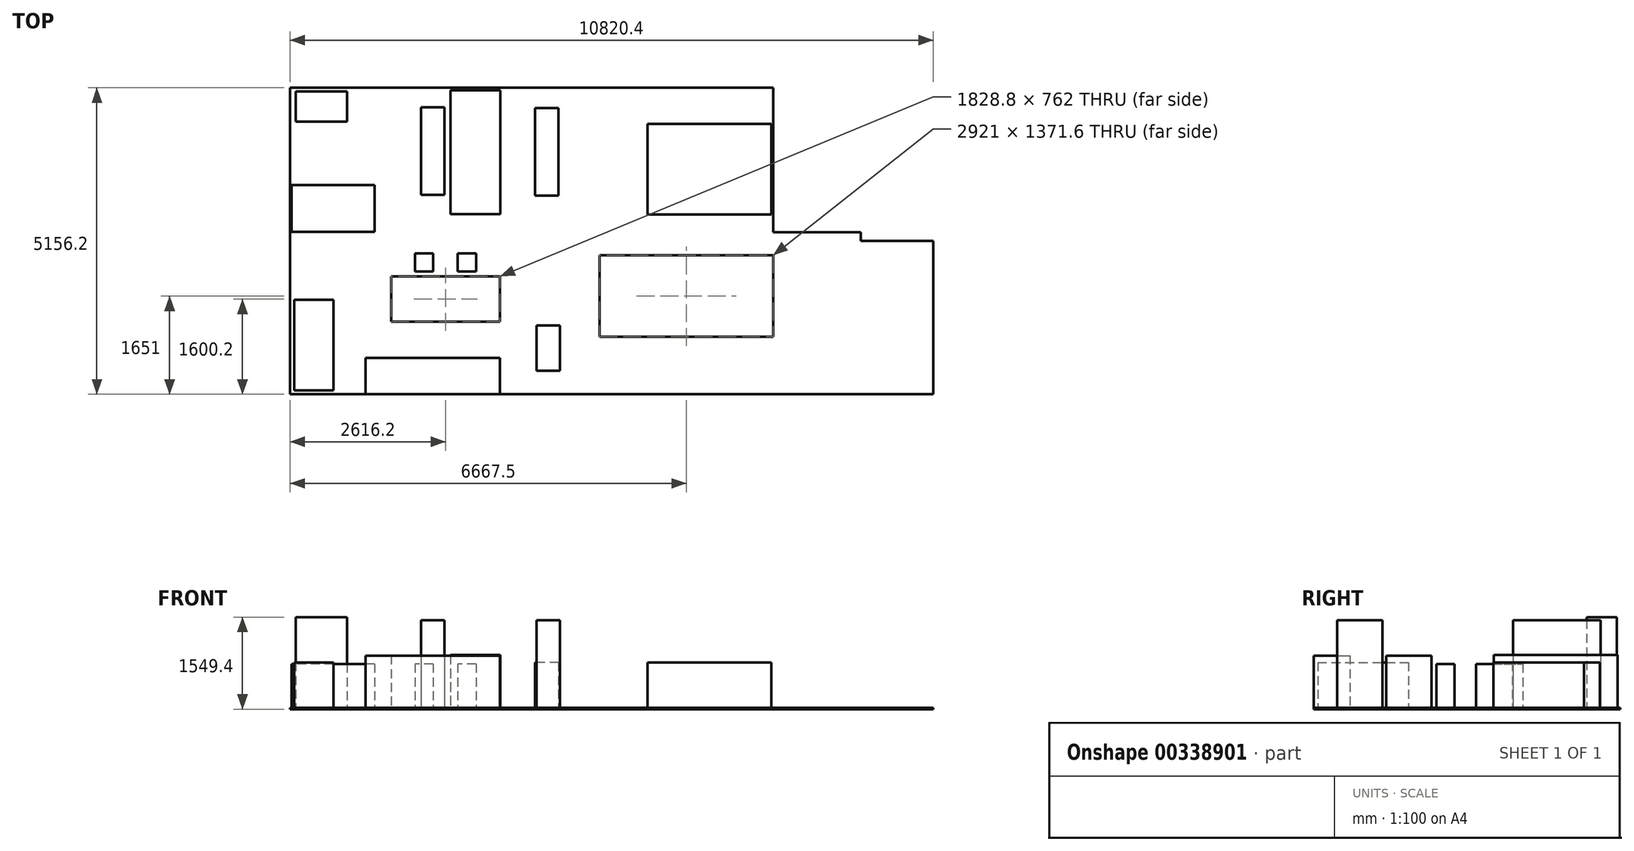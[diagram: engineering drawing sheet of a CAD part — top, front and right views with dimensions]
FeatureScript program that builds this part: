
annotation { "Feature Type Name" : "Feature", "Feature Type Description" : "" }
export const myFeature = defineFeature(function(context is Context, id is Id, definition is map)
    precondition{}
    {
        {
            var Q0;
            Q0=qCreatedBy(makeId("Top.planeOp"),FACE);
            var sketch = newSketch(context, id + "F0", { "sketchPlane" : qUnion([Q0])});
            skLineSegment(sketch, "E0.bottom", {"start": v(4800.6, -2578.1) * mm, "end": v(-812.8, -2578.1) * mm});
            skLineSegment(sketch, "E0.top", {"start": v(3327.4, 2578.1) * mm, "end": v(-4800.6, 2578.1) * mm});
            skLineSegment(sketch, "E0.left", {"start": v(4800.6, -2578.1) * mm, "end": v(4800.6, 0) * mm});
            skLineSegment(sketch, "E0.right", {"start": v(-4800.6, -2578.1) * mm, "end": v(-4800.6, 2578.1) * mm});
            skPoint(sketch, "E0.middle", {"position": v(0, 0) * mm});
            skLineSegment(sketch, "E1", {"start": v(-203.2, 2578.1) * mm, "end": v(-203.2, 139.7) * mm});
            skLineSegment(sketch, "E2", {"start": v(-203.2, 139.7) * mm, "end": v(406.4, 139.7) * mm});
            skLineSegment(sketch, "E3", {"start": v(406.4, 139.7) * mm, "end": v(406.4, 2578.1) * mm});
            skLineSegment(sketch, "E4", {"start": v(-1270, -2578.1) * mm, "end": v(-1270, -952.5) * mm});
            skLineSegment(sketch, "E5", {"start": v(-1270, -952.5) * mm, "end": v(-812.8, -952.5) * mm});
            skLineSegment(sketch, "E6", {"start": v(-812.8, -952.5) * mm, "end": v(-812.8, -2578.1) * mm});
            skLineSegment(sketch, "E7", {"start": v(4800.6, -2578.1) * mm, "end": v(6019.8, -2578.1) * mm});
            skLineSegment(sketch, "E8", {"start": v(6019.8, -2578.1) * mm, "end": v(6019.8, 0) * mm});
            skLineSegment(sketch, "E9", {"start": v(6019.8, 0) * mm, "end": v(4800.6, 0) * mm});
            skLineSegment(sketch, "E10", {"start": v(406.4, 139.7) * mm, "end": v(406.4, -1612.9) * mm});
            skLineSegment(sketch, "E11", {"start": v(406.4, -1612.9) * mm, "end": v(4800.6, -1612.9) * mm});
            skLineSegment(sketch, "E12", {"start": v(-1270, -952.5) * mm, "end": v(-1270, -596.9) * mm});
            skLineSegment(sketch, "E13", {"start": v(-1270, -596.9) * mm, "end": v(-3098.8, -596.9) * mm});
            skLineSegment(sketch, "E14", {"start": v(-3098.8, -596.9) * mm, "end": v(-3098.8, -1358.9) * mm});
            skLineSegment(sketch, "E15", {"start": v(-3098.8, -1358.9) * mm, "end": v(-1270, -1358.9) * mm});
            skLineSegment(sketch, "E16", {"start": v(-3530.6, -2578.1) * mm, "end": v(-3530.6, -1968.5) * mm});
            skLineSegment(sketch, "E17", {"start": v(-3530.6, -1968.5) * mm, "end": v(-1270, -1968.5) * mm});
            skLineSegment(sketch, "E18", {"start": v(3327.4, -1612.9) * mm, "end": v(3327.4, 144.58) * mm});
            skLineSegment(sketch, "E19", {"start": v(3327.4, 144.58) * mm, "end": v(3327.4, 144.58) * mm});
            skPoint(sketch, "E20.orphan", {"position": v(4800.6, 2578.1) * mm});
            skLineSegment(sketch, "E21", {"start": v(3327.4, 144.58) * mm, "end": v(4800.6, 144.58) * mm});
            skLineSegment(sketch, "E22", {"start": v(4800.6, 0) * mm, "end": v(4800.6, 144.58) * mm});
            skLineSegment(sketch, "E23", {"start": v(-812.8, -2578.1) * mm, "end": v(-1270, -2578.1) * mm});
            skLineSegment(sketch, "E24", {"start": v(-1270, -2578.1) * mm, "end": v(-4800.6, -2578.1) * mm});
            skLineSegment(sketch, "E25", {"start": v(3327.4, 144.58) * mm, "end": v(3327.4, 2578.1) * mm});
            skLineSegment(sketch, "E26", {"start": v(406.4, 139.7) * mm, "end": v(406.4, 139.7) * mm});
            skLineSegment(sketch, "E27", {"start": v(406.4, -241.3) * mm, "end": v(3327.4, -241.3) * mm});
            skPoint(sketch, "E27.endSnap0", {"position": v(3327.4, -734.16) * mm});
            skSolve(sketch);
        }
        {
            var Q0;
            Q0=sQuery(id+"F0.wireOp",EDGE,"E0.top");
            var Q1;
            Q1=sQuery(id+"F0.wireOp",EDGE,"E0.right");
            var Q2;
            Q2=sQuery(id+"F0.wireOp",EDGE,"E24");
            var Q3;
            Q3=sQuery(id+"F0.wireOp",EDGE,"E4");
            var Q4;
            Q4=sQuery(id+"F0.wireOp",EDGE,"E5");
            var Q5;
            Q5=sQuery(id+"F0.wireOp",EDGE,"E6");
            var Q6;
            Q6=sQuery(id+"F0.wireOp",EDGE,"E0.bottom");
            var Q7;
            Q7=sQuery(id+"F0.wireOp",EDGE,"E7");
            var Q8;
            Q8=sQuery(id+"F0.wireOp",EDGE,"E8");
            var Q9;
            Q9=sQuery(id+"F0.wireOp",EDGE,"E9");
            var Q10;
            Q10=sQuery(id+"F0.wireOp",EDGE,"E22");
            var Q11;
            Q11=sQuery(id+"F0.wireOp",EDGE,"E21");
            var Q12;
            Q12=sQuery(id+"F0.wireOp",EDGE,"E25");
            extrude(context, id + "F1", {"bodyType" : ToolBodyType.SURFACE, "surfaceEntities" : qUnion([Q0, Q1, Q2, Q3, Q4, Q5, Q6, Q7, Q8, Q9, Q10, Q11, Q12]), "depth" : 2133.6 * mm});
        }
        {
            var Q0;
            {var subQ0=sQuery(id+"F0.wireOp",EDGE,"E12");Q0=makeQuery(id+"F0.imprint","IMPRINT",FACE,{"disambiguationData":[TD([[makeQuery(id+"F0.imprint","IMPRINT",EDGE,{"derivedFrom":subQ0}),1.0]])]});}
            var Q1;
            {var subQ4=sQuery(id+"F0.wireOp",EDGE,"E16");Q1=makeQuery(id+"F0.imprint","IMPRINT",FACE,{"disambiguationData":[TD([[makeQuery(id+"F0.imprint","IMPRINT",EDGE,{"derivedFrom":subQ4}),-1.0]])]});}
            extrude(context, id + "F2", {"entities" : qUnion([Q0, Q1]), "depth" : 901.7 * mm});
        }
        {
            var Q0;
            Q0=sQuery(id+"F0.wireOp",EDGE,"E1");
            var Q1;
            Q1=sQuery(id+"F0.wireOp",EDGE,"E2");
            var Q2;
            Q2=sQuery(id+"F0.wireOp",EDGE,"E3");
            extrude(context, id + "F3", {"bodyType" : ToolBodyType.SURFACE, "surfaceEntities" : qUnion([Q0, Q1, Q2]), "depth" : 2133.6 * mm});
        }
        {
            var Q0;
            Q0 = qSketchRegion(id + "F0", true);
            extrude(context, id + "F4", {"entities" : qUnion([Q0]), "depth" : 25.4 * mm});
        }
        {
            var Q0;
            Q0=sQuery(id+"F0.wireOp",EDGE,"E10");
            var Q1;
            Q1=sQuery(id+"F0.wireOp",EDGE,"E11");
            extrude(context, id + "F5", {"bodyType" : ToolBodyType.SURFACE, "surfaceEntities" : qUnion([Q0, Q1]), "depth" : 2133.6 * mm});
        }
        {
            var Q0;
            Q0=sQuery(id+"F0.wireOp",EDGE,"E18");
            extrude(context, id + "F6", {"bodyType" : ToolBodyType.SURFACE, "surfaceEntities" : qUnion([Q0]), "depth" : 2133.6 * mm});
        }
        {
            var Q0;
            Q0=makeQuery(id+"F4.opExtrude","CAP_FACE",FACE,{"disambiguationData":[OSD([sQuery(id+"F0.wireOp",EDGE,"E0.bottom"),sQuery(id+"F0.wireOp",EDGE,"E0.top"),sQuery(id+"F0.wireOp",EDGE,"E0.right"),sQuery(id+"F0.wireOp",EDGE,"E4"),sQuery(id+"F0.wireOp",EDGE,"E7"),sQuery(id+"F0.wireOp",EDGE,"E8"),sQuery(id+"F0.wireOp",EDGE,"E9"),sQuery(id+"F0.wireOp",EDGE,"E12"),sQuery(id+"F0.wireOp",EDGE,"E13"),sQuery(id+"F0.wireOp",EDGE,"E14"),sQuery(id+"F0.wireOp",EDGE,"E15"),sQuery(id+"F0.wireOp",EDGE,"E21"),sQuery(id+"F0.wireOp",EDGE,"E22"),sQuery(id+"F0.wireOp",EDGE,"E23"),sQuery(id+"F0.wireOp",EDGE,"E24"),sQuery(id+"F0.wireOp",EDGE,"E25")])],"isStart":false});
            var sketch = newSketch(context, id + "F7", { "sketchPlane" : qUnion([Q0])});
            skLineSegment(sketch, "E28.bottom", {"start": v(-1265.13, 450.06) * mm, "end": v(-2103.33, 450.06) * mm});
            skLineSegment(sketch, "E28.top", {"start": v(-1265.13, 2532.86) * mm, "end": v(-2103.33, 2532.86) * mm});
            skLineSegment(sketch, "E28.left", {"start": v(-1265.13, 450.06) * mm, "end": v(-1265.13, 2532.86) * mm});
            skLineSegment(sketch, "E28.right", {"start": v(-2103.33, 450.06) * mm, "end": v(-2103.33, 2532.86) * mm});
            skPoint(sketch, "E28.middle", {"position": v(-1684.23, 1491.46) * mm});
            skSolve(sketch);
        }
        {
            var Q0;
            Q0=makeQuery(id+"F7.imprint","IMPRINT",FACE,{"disambiguationData":[TD([[makeQuery(id+"F7.imprint","IMPRINT",EDGE,{"derivedFrom":sQuery(id+"F7.wireOp",EDGE,"E28.bottom")}),-1.0]])]});
            extrude(context, id + "F8", {"entities" : qUnion([Q0]), "depth" : 889 * mm});
        }
        {
            var Q0;
            Q0=makeQuery(id+"F4.opExtrude","CAP_FACE",FACE,{"disambiguationData":[OSD([sQuery(id+"F0.wireOp",EDGE,"E0.bottom"),sQuery(id+"F0.wireOp",EDGE,"E0.top"),sQuery(id+"F0.wireOp",EDGE,"E0.right"),sQuery(id+"F0.wireOp",EDGE,"E4"),sQuery(id+"F0.wireOp",EDGE,"E7"),sQuery(id+"F0.wireOp",EDGE,"E8"),sQuery(id+"F0.wireOp",EDGE,"E9"),sQuery(id+"F0.wireOp",EDGE,"E12"),sQuery(id+"F0.wireOp",EDGE,"E13"),sQuery(id+"F0.wireOp",EDGE,"E14"),sQuery(id+"F0.wireOp",EDGE,"E15"),sQuery(id+"F0.wireOp",EDGE,"E21"),sQuery(id+"F0.wireOp",EDGE,"E22"),sQuery(id+"F0.wireOp",EDGE,"E23"),sQuery(id+"F0.wireOp",EDGE,"E24"),sQuery(id+"F0.wireOp",EDGE,"E25")])],"isStart":false});
            var sketch = newSketch(context, id + "F9", { "sketchPlane" : qUnion([Q0])});
            skLineSegment(sketch, "E29.bottom", {"start": v(-284.43, 761.48) * mm, "end": v(-678.13, 761.48) * mm});
            skLineSegment(sketch, "E29.top", {"start": v(-284.43, 2234.68) * mm, "end": v(-678.13, 2234.68) * mm});
            skLineSegment(sketch, "E29.left", {"start": v(-284.43, 761.48) * mm, "end": v(-284.43, 2234.68) * mm});
            skLineSegment(sketch, "E29.right", {"start": v(-678.13, 761.48) * mm, "end": v(-678.13, 2234.68) * mm});
            skPoint(sketch, "E29.middle", {"position": v(-481.28, 1498.08) * mm});
            skSolve(sketch);
        }
        {
            var Q0;
            Q0=makeQuery(id+"F9.imprint","IMPRINT",FACE,{"disambiguationData":[TD([[makeQuery(id+"F9.imprint","IMPRINT",EDGE,{"derivedFrom":sQuery(id+"F9.wireOp",EDGE,"E29.bottom")}),-1.0]])]});
            extrude(context, id + "F10", {"entities" : qUnion([Q0]), "depth" : 762 * mm});
        }
        {
            var Q0;
            Q0=makeQuery(id+"F4.opExtrude","CAP_FACE",FACE,{"disambiguationData":[OSD([sQuery(id+"F0.wireOp",EDGE,"E0.bottom"),sQuery(id+"F0.wireOp",EDGE,"E0.top"),sQuery(id+"F0.wireOp",EDGE,"E0.right"),sQuery(id+"F0.wireOp",EDGE,"E4"),sQuery(id+"F0.wireOp",EDGE,"E7"),sQuery(id+"F0.wireOp",EDGE,"E8"),sQuery(id+"F0.wireOp",EDGE,"E9"),sQuery(id+"F0.wireOp",EDGE,"E12"),sQuery(id+"F0.wireOp",EDGE,"E13"),sQuery(id+"F0.wireOp",EDGE,"E14"),sQuery(id+"F0.wireOp",EDGE,"E15"),sQuery(id+"F0.wireOp",EDGE,"E21"),sQuery(id+"F0.wireOp",EDGE,"E22"),sQuery(id+"F0.wireOp",EDGE,"E23"),sQuery(id+"F0.wireOp",EDGE,"E24"),sQuery(id+"F0.wireOp",EDGE,"E25")])],"isStart":false});
            var sketch = newSketch(context, id + "F11", { "sketchPlane" : qUnion([Q0])});
            skLineSegment(sketch, "E30.bottom", {"start": v(-3841.87, 2010.92) * mm, "end": v(-4705.47, 2010.92) * mm});
            skLineSegment(sketch, "E30.top", {"start": v(-3841.87, 2518.92) * mm, "end": v(-4705.47, 2518.92) * mm});
            skLineSegment(sketch, "E30.left", {"start": v(-3841.87, 2010.92) * mm, "end": v(-3841.87, 2518.92) * mm});
            skLineSegment(sketch, "E30.right", {"start": v(-4705.47, 2010.92) * mm, "end": v(-4705.47, 2518.92) * mm});
            skPoint(sketch, "E30.middle", {"position": v(-4273.67, 2264.92) * mm});
            skSolve(sketch);
        }
        {
            var Q0;
            Q0=makeQuery(id+"F11.imprint","IMPRINT",FACE,{"disambiguationData":[TD([[makeQuery(id+"F11.imprint","IMPRINT",EDGE,{"derivedFrom":sQuery(id+"F11.wireOp",EDGE,"E30.bottom")}),-1.0]])]});
            extrude(context, id + "F12", {"entities" : qUnion([Q0]), "depth" : 1524 * mm});
        }
        {
            var Q0;
            Q0=makeQuery(id+"F4.opExtrude","CAP_FACE",FACE,{"disambiguationData":[OSD([sQuery(id+"F0.wireOp",EDGE,"E0.bottom"),sQuery(id+"F0.wireOp",EDGE,"E0.top"),sQuery(id+"F0.wireOp",EDGE,"E0.right"),sQuery(id+"F0.wireOp",EDGE,"E4"),sQuery(id+"F0.wireOp",EDGE,"E7"),sQuery(id+"F0.wireOp",EDGE,"E8"),sQuery(id+"F0.wireOp",EDGE,"E9"),sQuery(id+"F0.wireOp",EDGE,"E12"),sQuery(id+"F0.wireOp",EDGE,"E13"),sQuery(id+"F0.wireOp",EDGE,"E14"),sQuery(id+"F0.wireOp",EDGE,"E15"),sQuery(id+"F0.wireOp",EDGE,"E21"),sQuery(id+"F0.wireOp",EDGE,"E22"),sQuery(id+"F0.wireOp",EDGE,"E23"),sQuery(id+"F0.wireOp",EDGE,"E24"),sQuery(id+"F0.wireOp",EDGE,"E25")])],"isStart":false});
            var sketch = newSketch(context, id + "F13", { "sketchPlane" : qUnion([Q0])});
            skLineSegment(sketch, "E31.bottom", {"start": v(-3376.72, 151.52) * mm, "end": v(-4773.72, 151.52) * mm});
            skLineSegment(sketch, "E31.top", {"start": v(-3376.72, 938.92) * mm, "end": v(-4773.72, 938.92) * mm});
            skLineSegment(sketch, "E31.left", {"start": v(-3376.72, 151.52) * mm, "end": v(-3376.72, 938.92) * mm});
            skLineSegment(sketch, "E31.right", {"start": v(-4773.72, 151.52) * mm, "end": v(-4773.72, 938.92) * mm});
            skPoint(sketch, "E31.middle", {"position": v(-4075.22, 545.22) * mm});
            skSolve(sketch);
        }
        {
            var Q0;
            Q0=makeQuery(id+"F13.imprint","IMPRINT",FACE,{"disambiguationData":[TD([[makeQuery(id+"F13.imprint","IMPRINT",EDGE,{"derivedFrom":sQuery(id+"F13.wireOp",EDGE,"E31.bottom")}),-1.0]])]});
            extrude(context, id + "F14", {"entities" : qUnion([Q0]), "depth" : 736.6 * mm});
        }
        {
            var Q0;
            Q0=makeQuery(id+"F4.opExtrude","CAP_FACE",FACE,{"disambiguationData":[OSD([sQuery(id+"F0.wireOp",EDGE,"E0.bottom"),sQuery(id+"F0.wireOp",EDGE,"E0.top"),sQuery(id+"F0.wireOp",EDGE,"E0.right"),sQuery(id+"F0.wireOp",EDGE,"E4"),sQuery(id+"F0.wireOp",EDGE,"E7"),sQuery(id+"F0.wireOp",EDGE,"E8"),sQuery(id+"F0.wireOp",EDGE,"E9"),sQuery(id+"F0.wireOp",EDGE,"E12"),sQuery(id+"F0.wireOp",EDGE,"E13"),sQuery(id+"F0.wireOp",EDGE,"E14"),sQuery(id+"F0.wireOp",EDGE,"E15"),sQuery(id+"F0.wireOp",EDGE,"E21"),sQuery(id+"F0.wireOp",EDGE,"E22"),sQuery(id+"F0.wireOp",EDGE,"E23"),sQuery(id+"F0.wireOp",EDGE,"E24"),sQuery(id+"F0.wireOp",EDGE,"E25")])],"isStart":false});
            var sketch = newSketch(context, id + "F15", { "sketchPlane" : qUnion([Q0])});
            skLineSegment(sketch, "E32.bottom", {"start": v(-259.52, -2184.38) * mm, "end": v(-653.22, -2184.38) * mm});
            skLineSegment(sketch, "E32.top", {"start": v(-259.52, -1422.38) * mm, "end": v(-653.22, -1422.38) * mm});
            skLineSegment(sketch, "E32.left", {"start": v(-259.52, -2184.38) * mm, "end": v(-259.52, -1422.38) * mm});
            skLineSegment(sketch, "E32.right", {"start": v(-653.22, -2184.38) * mm, "end": v(-653.22, -1422.38) * mm});
            skPoint(sketch, "E32.middle", {"position": v(-456.37, -1803.38) * mm});
            skSolve(sketch);
        }
        {
            var Q0;
            Q0=makeQuery(id+"F15.imprint","IMPRINT",FACE,{"disambiguationData":[TD([[makeQuery(id+"F15.imprint","IMPRINT",EDGE,{"derivedFrom":sQuery(id+"F15.wireOp",EDGE,"E32.bottom")}),-1.0]])]});
            extrude(context, id + "F16", {"entities" : qUnion([Q0]), "depth" : 1473.2 * mm});
        }
        {
            var Q0;
            Q0=makeQuery(id+"F4.opExtrude","CAP_FACE",FACE,{"disambiguationData":[OSD([sQuery(id+"F0.wireOp",EDGE,"E0.bottom"),sQuery(id+"F0.wireOp",EDGE,"E0.top"),sQuery(id+"F0.wireOp",EDGE,"E0.right"),sQuery(id+"F0.wireOp",EDGE,"E4"),sQuery(id+"F0.wireOp",EDGE,"E7"),sQuery(id+"F0.wireOp",EDGE,"E8"),sQuery(id+"F0.wireOp",EDGE,"E9"),sQuery(id+"F0.wireOp",EDGE,"E10"),sQuery(id+"F0.wireOp",EDGE,"E11"),sQuery(id+"F0.wireOp",EDGE,"E12"),sQuery(id+"F0.wireOp",EDGE,"E13"),sQuery(id+"F0.wireOp",EDGE,"E14"),sQuery(id+"F0.wireOp",EDGE,"E15"),sQuery(id+"F0.wireOp",EDGE,"E18"),sQuery(id+"F0.wireOp",EDGE,"E21"),sQuery(id+"F0.wireOp",EDGE,"E22"),sQuery(id+"F0.wireOp",EDGE,"E23"),sQuery(id+"F0.wireOp",EDGE,"E24"),sQuery(id+"F0.wireOp",EDGE,"E25"),sQuery(id+"F0.wireOp",EDGE,"E27")])],"isStart":false});
            var sketch = newSketch(context, id + "F17", { "sketchPlane" : qUnion([Q0])});
            skLineSegment(sketch, "E33.bottom", {"start": v(-2200.56, 773.8) * mm, "end": v(-2594.26, 773.8) * mm});
            skLineSegment(sketch, "E33.top", {"start": v(-2200.56, 2247) * mm, "end": v(-2594.26, 2247) * mm});
            skLineSegment(sketch, "E33.left", {"start": v(-2200.56, 773.8) * mm, "end": v(-2200.56, 2247) * mm});
            skLineSegment(sketch, "E33.right", {"start": v(-2594.26, 773.8) * mm, "end": v(-2594.26, 2247) * mm});
            skPoint(sketch, "E33.middle", {"position": v(-2397.41, 1510.4) * mm});
            skSolve(sketch);
        }
        {
            var Q0;
            Q0=makeQuery(id+"F17.imprint","IMPRINT",FACE,{"disambiguationData":[TD([[makeQuery(id+"F17.imprint","IMPRINT",EDGE,{"derivedFrom":sQuery(id+"F17.wireOp",EDGE,"E33.bottom")}),-1.0]])]});
            var Q1;
            Q1=sQuery(id+"F17.wireOp",EDGE,"E33.left");
            extrude(context, id + "F18", {"entities" : qUnion([Q0]), "surfaceEntities" : qUnion([Q1]), "depth" : 1473.2 * mm});
        }
        {
            var Q0;
            Q0=makeQuery(id+"F4.opExtrude","CAP_FACE",FACE,{"disambiguationData":[OSD([sQuery(id+"F0.wireOp",EDGE,"E0.bottom"),sQuery(id+"F0.wireOp",EDGE,"E0.top"),sQuery(id+"F0.wireOp",EDGE,"E0.right"),sQuery(id+"F0.wireOp",EDGE,"E4"),sQuery(id+"F0.wireOp",EDGE,"E7"),sQuery(id+"F0.wireOp",EDGE,"E8"),sQuery(id+"F0.wireOp",EDGE,"E9"),sQuery(id+"F0.wireOp",EDGE,"E10"),sQuery(id+"F0.wireOp",EDGE,"E11"),sQuery(id+"F0.wireOp",EDGE,"E12"),sQuery(id+"F0.wireOp",EDGE,"E13"),sQuery(id+"F0.wireOp",EDGE,"E14"),sQuery(id+"F0.wireOp",EDGE,"E15"),sQuery(id+"F0.wireOp",EDGE,"E18"),sQuery(id+"F0.wireOp",EDGE,"E21"),sQuery(id+"F0.wireOp",EDGE,"E22"),sQuery(id+"F0.wireOp",EDGE,"E23"),sQuery(id+"F0.wireOp",EDGE,"E24"),sQuery(id+"F0.wireOp",EDGE,"E25"),sQuery(id+"F0.wireOp",EDGE,"E27")])],"isStart":false});
            var sketch = newSketch(context, id + "F19", { "sketchPlane" : qUnion([Q0])});
            skLineSegment(sketch, "E34.bottom", {"start": v(-2394.14, -515.6) * mm, "end": v(-2698.94, -515.6) * mm});
            skLineSegment(sketch, "E34.top", {"start": v(-2394.14, -210.8) * mm, "end": v(-2698.94, -210.8) * mm});
            skLineSegment(sketch, "E34.left", {"start": v(-2394.14, -515.6) * mm, "end": v(-2394.14, -210.8) * mm});
            skLineSegment(sketch, "E34.right", {"start": v(-2698.94, -515.6) * mm, "end": v(-2698.94, -210.8) * mm});
            skPoint(sketch, "E34.middle", {"position": v(-2546.54, -363.2) * mm});
            skLineSegment(sketch, "E35.bottom", {"start": v(-1672.78, -515.6) * mm, "end": v(-1977.58, -515.6) * mm});
            skLineSegment(sketch, "E35.top", {"start": v(-1672.78, -210.8) * mm, "end": v(-1977.58, -210.8) * mm});
            skLineSegment(sketch, "E35.left", {"start": v(-1672.78, -515.6) * mm, "end": v(-1672.78, -210.8) * mm});
            skLineSegment(sketch, "E35.right", {"start": v(-1977.58, -515.6) * mm, "end": v(-1977.58, -210.8) * mm});
            skPoint(sketch, "E35.middle", {"position": v(-1825.18, -363.2) * mm});
            skPoint(sketch, "E35.middle.positionSnap0", {"position": v(-2394.14, -363.2) * mm});
            skPoint(sketch, "E35.cornerSnap0", {"position": v(-2546.54, -515.6) * mm});
            skPoint(sketch, "E35.centerSnap0", {"position": v(-2394.14, -363.2) * mm});
            skSolve(sketch);
        }
        {
            var Q0;
            Q0=makeQuery(id+"F19.imprint","IMPRINT",FACE,{"disambiguationData":[TD([[makeQuery(id+"F19.imprint","IMPRINT",EDGE,{"derivedFrom":sQuery(id+"F19.wireOp",EDGE,"E35.bottom")}),-1.0]])]});
            var Q1;
            Q1=makeQuery(id+"F19.imprint","IMPRINT",FACE,{"disambiguationData":[TD([[makeQuery(id+"F19.imprint","IMPRINT",EDGE,{"derivedFrom":sQuery(id+"F19.wireOp",EDGE,"E34.bottom")}),-1.0]])]});
            extrude(context, id + "F20", {"entities" : qUnion([Q0, Q1]), "depth" : 736.6 * mm});
        }
        {
            var Q0;
            Q0=makeQuery(id+"F4.opExtrude","CAP_FACE",FACE,{"disambiguationData":[OSD([sQuery(id+"F0.wireOp",EDGE,"E0.bottom"),sQuery(id+"F0.wireOp",EDGE,"E0.top"),sQuery(id+"F0.wireOp",EDGE,"E0.right"),sQuery(id+"F0.wireOp",EDGE,"E4"),sQuery(id+"F0.wireOp",EDGE,"E7"),sQuery(id+"F0.wireOp",EDGE,"E8"),sQuery(id+"F0.wireOp",EDGE,"E9"),sQuery(id+"F0.wireOp",EDGE,"E10"),sQuery(id+"F0.wireOp",EDGE,"E11"),sQuery(id+"F0.wireOp",EDGE,"E12"),sQuery(id+"F0.wireOp",EDGE,"E13"),sQuery(id+"F0.wireOp",EDGE,"E14"),sQuery(id+"F0.wireOp",EDGE,"E15"),sQuery(id+"F0.wireOp",EDGE,"E18"),sQuery(id+"F0.wireOp",EDGE,"E21"),sQuery(id+"F0.wireOp",EDGE,"E22"),sQuery(id+"F0.wireOp",EDGE,"E23"),sQuery(id+"F0.wireOp",EDGE,"E24"),sQuery(id+"F0.wireOp",EDGE,"E25"),sQuery(id+"F0.wireOp",EDGE,"E27")])],"isStart":false});
            var sketch = newSketch(context, id + "F21", { "sketchPlane" : qUnion([Q0])});
            skLineSegment(sketch, "E36.bottom", {"start": v(-4072.6, -2513) * mm, "end": v(-4733, -2513) * mm});
            skLineSegment(sketch, "E36.top", {"start": v(-4072.6, -989) * mm, "end": v(-4733, -989) * mm});
            skLineSegment(sketch, "E36.left", {"start": v(-4072.6, -2513) * mm, "end": v(-4072.6, -989) * mm});
            skLineSegment(sketch, "E36.right", {"start": v(-4733, -2513) * mm, "end": v(-4733, -989) * mm});
            skPoint(sketch, "E36.middle", {"position": v(-4402.8, -1751) * mm});
            skSolve(sketch);
        }
        {
            var Q0;
            Q0=makeQuery(id+"F21.imprint","IMPRINT",FACE,{"disambiguationData":[TD([[makeQuery(id+"F21.imprint","IMPRINT",EDGE,{"derivedFrom":sQuery(id+"F21.wireOp",EDGE,"E36.bottom")}),-1.0]])]});
            extrude(context, id + "F22", {"entities" : qUnion([Q0]), "depth" : 762 * mm});
        }
        {
            var Q0;
            Q0=makeQuery(id+"F4.opExtrude","CAP_FACE",FACE,{"disambiguationData":[OSD([sQuery(id+"F0.wireOp",EDGE,"E0.bottom"),sQuery(id+"F0.wireOp",EDGE,"E0.top"),sQuery(id+"F0.wireOp",EDGE,"E0.right"),sQuery(id+"F0.wireOp",EDGE,"E4"),sQuery(id+"F0.wireOp",EDGE,"E7"),sQuery(id+"F0.wireOp",EDGE,"E8"),sQuery(id+"F0.wireOp",EDGE,"E9"),sQuery(id+"F0.wireOp",EDGE,"E10"),sQuery(id+"F0.wireOp",EDGE,"E11"),sQuery(id+"F0.wireOp",EDGE,"E12"),sQuery(id+"F0.wireOp",EDGE,"E13"),sQuery(id+"F0.wireOp",EDGE,"E14"),sQuery(id+"F0.wireOp",EDGE,"E15"),sQuery(id+"F0.wireOp",EDGE,"E18"),sQuery(id+"F0.wireOp",EDGE,"E21"),sQuery(id+"F0.wireOp",EDGE,"E22"),sQuery(id+"F0.wireOp",EDGE,"E23"),sQuery(id+"F0.wireOp",EDGE,"E24"),sQuery(id+"F0.wireOp",EDGE,"E25"),sQuery(id+"F0.wireOp",EDGE,"E27")])],"isStart":false});
            var sketch = newSketch(context, id + "F23", { "sketchPlane" : qUnion([Q0])});
            skLineSegment(sketch, "E37.bottom", {"start": v(3295.06, 444.5) * mm, "end": v(1212.26, 444.5) * mm});
            skLineSegment(sketch, "E37.top", {"start": v(3295.06, 1968.5) * mm, "end": v(1212.26, 1968.5) * mm});
            skLineSegment(sketch, "E37.left", {"start": v(3295.06, 444.5) * mm, "end": v(3295.06, 1968.5) * mm});
            skLineSegment(sketch, "E37.right", {"start": v(1212.26, 444.5) * mm, "end": v(1212.26, 1968.5) * mm});
            skPoint(sketch, "E37.middle", {"position": v(2253.66, 1206.5) * mm});
            skSolve(sketch);
        }
        {
            var Q0;
            Q0=makeQuery(id+"F23.imprint","IMPRINT",FACE,{"disambiguationData":[TD([[makeQuery(id+"F23.imprint","IMPRINT",EDGE,{"derivedFrom":sQuery(id+"F23.wireOp",EDGE,"E37.bottom")}),-1.0]])]});
            extrude(context, id + "F24", {"entities" : qUnion([Q0]), "depth" : 762 * mm});
        }
    });
